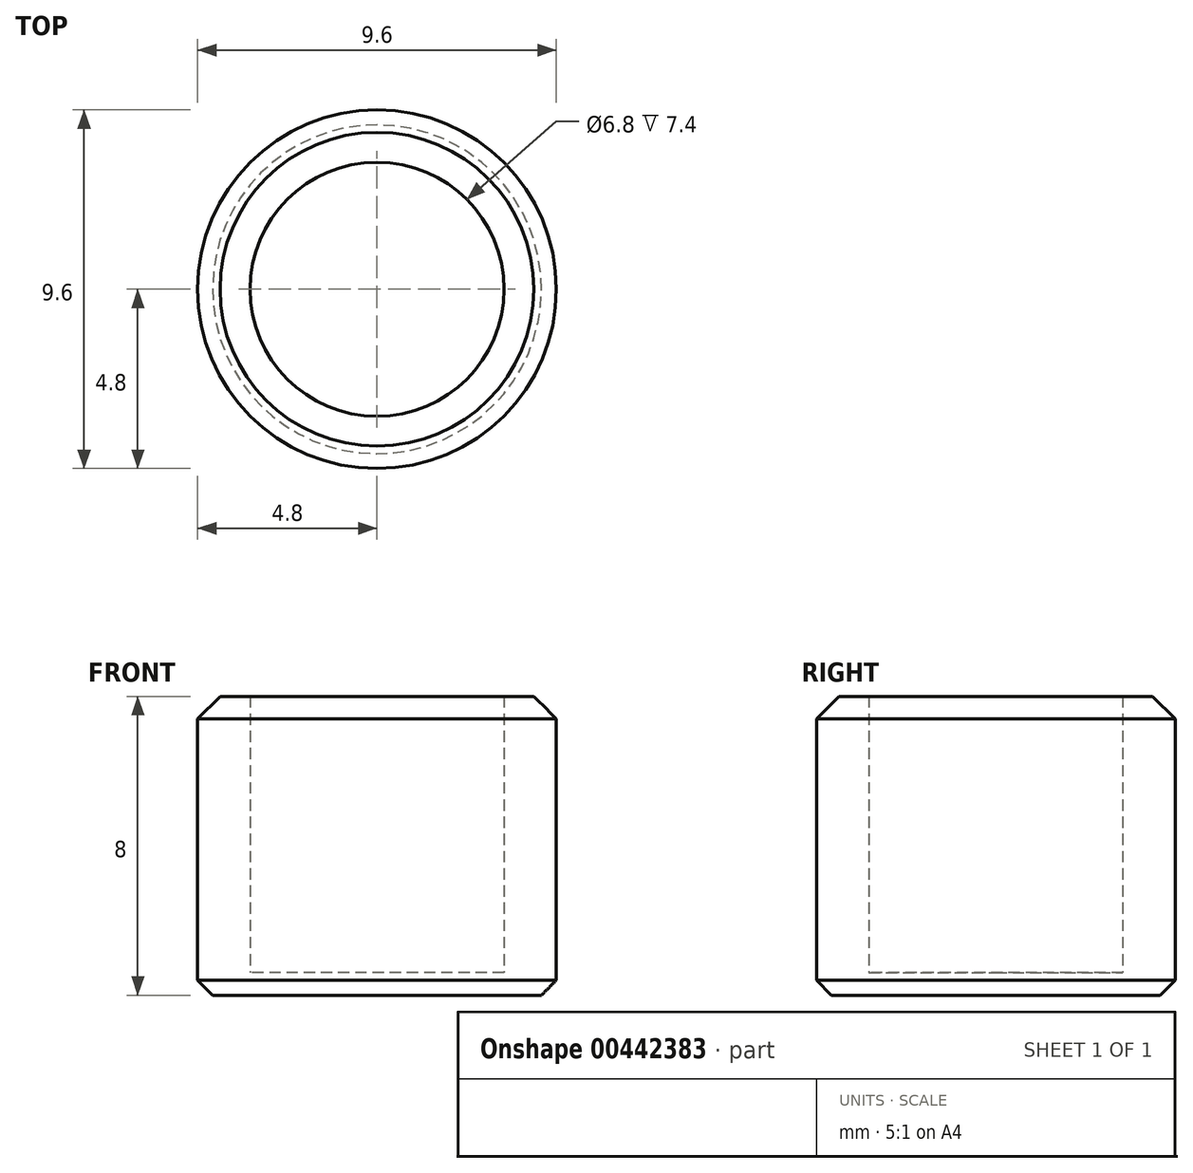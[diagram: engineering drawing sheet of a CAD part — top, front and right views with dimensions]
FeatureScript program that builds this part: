
annotation { "Feature Type Name" : "Feature", "Feature Type Description" : "" }
export const myFeature = defineFeature(function(context is Context, id is Id, definition is map)
    precondition{}
    {
        {
            var Q0;
            Q0=qCreatedBy(makeId("Top.planeOp"),FACE);
            var sketch = newSketch(context, id + "F0", { "sketchPlane" : qUnion([Q0])});
            skCircle(sketch, "E0", {"center": v(0, 0) * mm, "radius": 3.4 * mm});
            skCircle(sketch, "E1", {"center": v(0, 0) * mm, "radius": 4.8 * mm});
            skSolve(sketch);
        }
        {
            var Q0;
            Q0=makeQuery(id+"F0.imprint","IMPRINT",FACE,{"disambiguationData":[TD([[makeQuery(id+"F0.imprint","IMPRINT",EDGE,{"derivedFrom":sQuery(id+"F0.wireOp",EDGE,"E0")}),1.0]])]});
            extrude(context, id + "F1", {"entities" : qUnion([Q0]), "depth" : .6 * mm, "offsetDistance" : 25 * mm});
        }
        {
            var Q0;
            Q0=makeQuery(id+"F0.imprint","IMPRINT",FACE,{"disambiguationData":[TD([[makeQuery(id+"F0.imprint","IMPRINT",EDGE,{"derivedFrom":sQuery(id+"F0.wireOp",EDGE,"E0")}),-1.0]])]});
            extrude(context, id + "F2", {"entities" : qUnion([Q0]), "operationType" : NewBodyOperationType.ADD, "depth" : 8 * mm, "offsetDistance" : 25 * mm});
        }
        {
            var Q0;
            Q0=makeQuery(id+"F2.opExtrude","CAP_EDGE",EDGE,{"disambiguationData":[OSD([sQuery(id+"F0.wireOp",EDGE,"E1")])],"isStart":true});
            chamfer(context, id + "F3", {"entities" : qUnion([Q0]), "width" : .4 * mm, "tangentPropagation" : true});
        }
        {
            var Q0;
            Q0=makeQuery(id+"F2.opExtrude","CAP_EDGE",EDGE,{"disambiguationData":[OSD([sQuery(id+"F0.wireOp",EDGE,"E1")])],"isStart":false});
            chamfer(context, id + "F4", {"entities" : qUnion([Q0]), "width" : .6 * mm, "tangentPropagation" : true});
        }
    });
